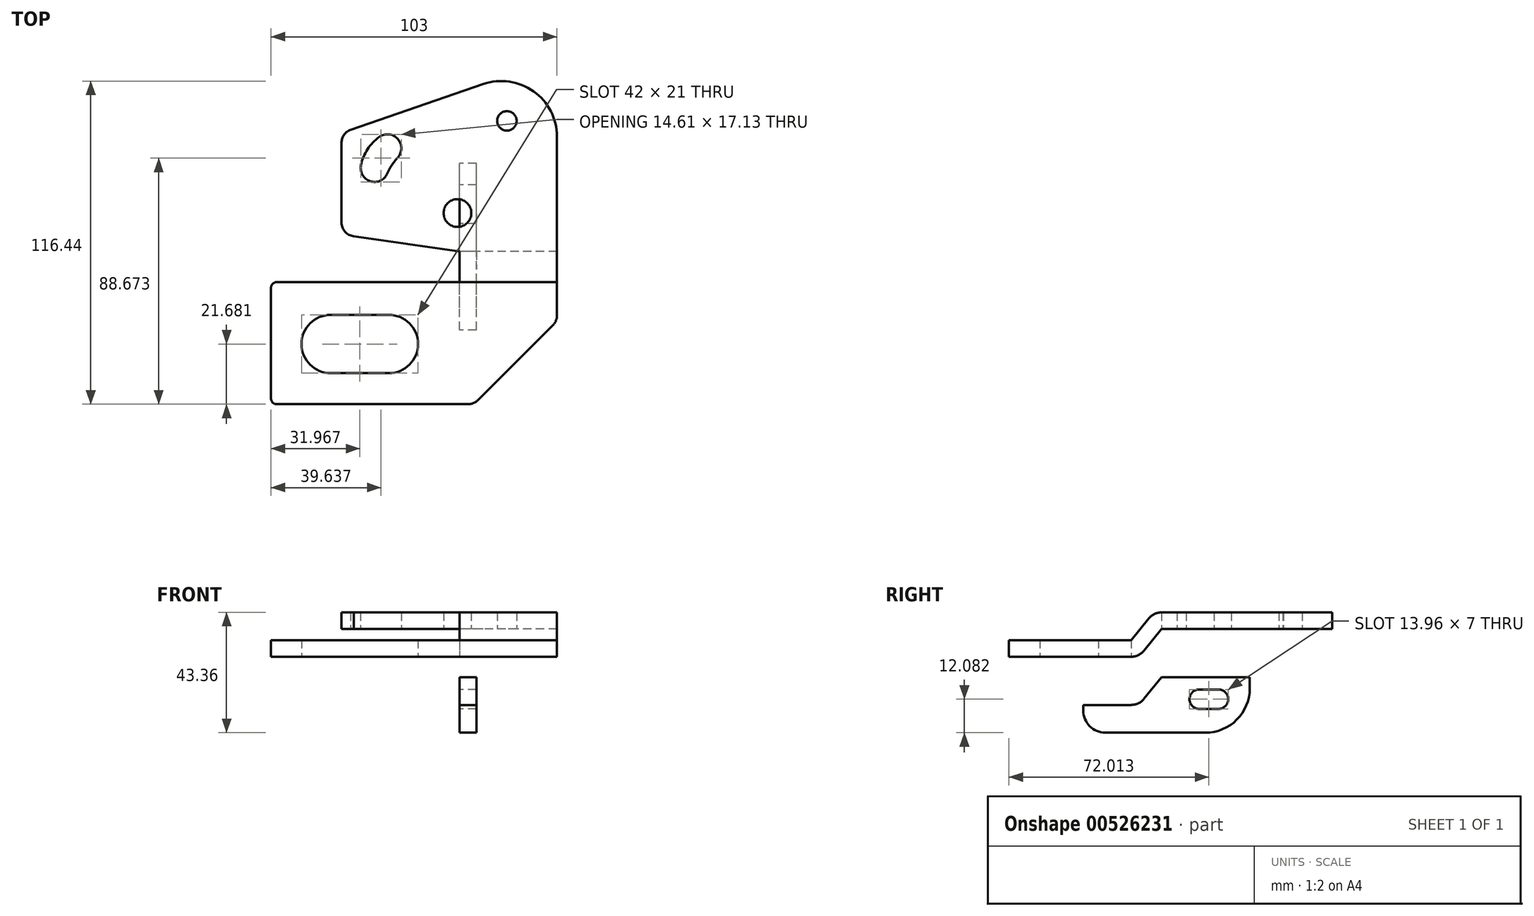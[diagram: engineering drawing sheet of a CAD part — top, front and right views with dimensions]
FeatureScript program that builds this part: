
annotation { "Feature Type Name" : "Feature", "Feature Type Description" : "" }
export const myFeature = defineFeature(function(context is Context, id is Id, definition is map)
    precondition{}
    {
        {
            var Q0;
            Q0=qCreatedBy(makeId("Top.planeOp"),FACE);
            var sketch = newSketch(context, id + "F0", { "sketchPlane" : qUnion([Q0])});
            skLineSegment(sketch, "E0.bottom", {"start": v(-65.96, -11) * mm, "end": v(0, -11) * mm});
            skLineSegment(sketch, "E0.top", {"start": v(-65.96, -55) * mm, "end": v(2.96, -55) * mm});
            skLineSegment(sketch, "E0.left", {"start": v(-67.96, -13) * mm, "end": v(-67.96, -53) * mm});
            skArc(sketch, "E1", {"start": v(-46.5, -22.82) * mm, "mid": v(-57, -33.32) * mm, "end": v(-46.5, -43.82) * mm});
            skArc(sketch, "E2", {"start": v(-25.5, -43.82) * mm, "mid": v(-15, -33.32) * mm, "end": v(-25.5, -22.82) * mm});
            skLineSegment(sketch, "E3", {"start": v(-46.5, -22.82) * mm, "end": v(-25.5, -22.82) * mm});
            skLineSegment(sketch, "E4", {"start": v(-46.5, -43.82) * mm, "end": v(-25.5, -43.82) * mm});
            skLineSegment(sketch, "E5", {"start": v(33.57, -26.5) * mm, "end": v(6.5, -53.54) * mm});
            skLineSegment(sketch, "E6", {"start": v(-42.58, 39.2) * mm, "end": v(-42.58, 10.48) * mm});
            skArc(sketch, "E7.filletArc", {"start": v(-42.58, 10.48) * mm, "mid": v(-41.3, 7.15) * mm, "end": v(-38.14, 5.51) * mm});
            skArc(sketch, "E8.filletArc", {"start": v(33.57, -26.5) * mm, "mid": v(34.66, -24.88) * mm, "end": v(35.04, -22.96) * mm});
            skLineSegment(sketch, "E9", {"start": v(8.51, 60.35) * mm, "end": v(-39.29, 43.9) * mm});
            skArc(sketch, "E10.filletArc", {"start": v(-39.29, 43.9) * mm, "mid": v(-41.67, 42.06) * mm, "end": v(-42.58, 39.2) * mm});
            skArc(sketch, "E11.filletArc", {"start": v(2.96, -55) * mm, "mid": v(4.88, -54.62) * mm, "end": v(6.5, -53.54) * mm});
            skCircle(sketch, "E12", {"center": v(-0.8, 13.88) * mm, "radius": 5 * mm});
            skArc(sketch, "E13", {"start": v(-35.57, 31.16) * mm, "mid": v(-32.23, 25.34) * mm, "end": v(-26.1, 28.1) * mm});
            skArc(sketch, "E14", {"start": v(-22.33, 33.89) * mm, "mid": v(-22.3, 40.6) * mm, "end": v(-28.96, 41.3) * mm});
            skArc(sketch, "E15", {"start": v(-28.96, 41.3) * mm, "mid": v(-33.2, 36.84) * mm, "end": v(-35.57, 31.16) * mm});
            skArc(sketch, "E16", {"start": v(-22.33, 33.89) * mm, "mid": v(-24.46, 31.15) * mm, "end": v(-26.1, 28.1) * mm});
            skCircle(sketch, "E17", {"center": v(17, 47.09) * mm, "radius": 3.5 * mm});
            skArc(sketch, "E18.filletArc", {"start": v(-65.96, -11) * mm, "mid": v(-67.37, -11.59) * mm, "end": v(-67.96, -13) * mm});
            skArc(sketch, "E19.filletArc", {"start": v(-67.96, -53) * mm, "mid": v(-67.37, -54.41) * mm, "end": v(-65.96, -55) * mm});
            skLineSegment(sketch, "E20.trimOffspring", {"start": v(-38.14, 5.51) * mm, "end": v(0, 0) * mm});
            skArc(sketch, "E21", {"start": v(35.02, 41.44) * mm, "mid": v(26.64, 57.72) * mm, "end": v(8.51, 60.35) * mm});
            skLineSegment(sketch, "E22", {"start": v(0, -11) * mm, "end": v(0, 0) * mm});
            skLineSegment(sketch, "E23", {"start": v(35.02, 41.44) * mm, "end": v(35.04, -22.96) * mm});
            skSolve(sketch);
        }
        {
            var Q0;
            Q0=qCreatedBy(makeId("Right.planeOp"),FACE);
            var sketch = newSketch(context, id + "F1", { "sketchPlane" : qUnion([Q0])});
            skLineSegment(sketch, "E24.right", {"start": v(79.89, 0) * mm, "end": v(79.89, -6) * mm});
            skLineSegment(sketch, "E25", {"start": v(-11, -10) * mm, "end": v(-11, -16) * mm});
            skLineSegment(sketch, "E26", {"start": v(0, -6) * mm, "end": v(0, 0) * mm});
            skLineSegment(sketch, "E27", {"start": v(0, 0) * mm, "end": v(0, -6) * mm});
            skLineSegment(sketch, "E28.trimOffspring", {"start": v(0, -6) * mm, "end": v(79.89, -6) * mm});
            skLineSegment(sketch, "E29.trimOffspring", {"start": v(0, 0) * mm, "end": v(79.89, 0) * mm});
            skArc(sketch, "E30", {"start": v(-11, -16) * mm, "mid": v(-8.43, -15.42) * mm, "end": v(-6.35, -13.8) * mm});
            skArc(sketch, "E31", {"start": v(0, 0) * mm, "mid": v(-2.57, -0.58) * mm, "end": v(-4.65, -2.2) * mm});
            skLineSegment(sketch, "E32", {"start": v(-11, -10) * mm, "end": v(-4.65, -2.2) * mm});
            skLineSegment(sketch, "E33", {"start": v(0, -6) * mm, "end": v(-6.35, -13.8) * mm});
            skLineSegment(sketch, "E34", {"start": v(-67.68, -10) * mm, "end": v(-67.68, -16) * mm});
            skLineSegment(sketch, "E35", {"start": v(-67.68, -16) * mm, "end": v(-11, -16) * mm});
            skLineSegment(sketch, "E36", {"start": v(-67.68, -10) * mm, "end": v(-11, -10) * mm});
            skLineSegment(sketch, "E37.trimOffspring", {"start": v(0, -23.36) * mm, "end": v(31.77, -23.36) * mm});
            skArc(sketch, "E38", {"start": v(-11, -33.36) * mm, "mid": v(-8.43, -32.77) * mm, "end": v(-6.35, -31.15) * mm});
            skLineSegment(sketch, "E39", {"start": v(0, -23.36) * mm, "end": v(-6.35, -31.15) * mm});
            skLineSegment(sketch, "E40", {"start": v(-28.23, -33.36) * mm, "end": v(-11, -33.36) * mm});
            skLineSegment(sketch, "E41", {"start": v(-28.23, -33.36) * mm, "end": v(-28.23, -35.36) * mm});
            skLineSegment(sketch, "E42", {"start": v(-20.23, -43.36) * mm, "end": v(15.77, -43.36) * mm});
            skArc(sketch, "E43.filletArc", {"start": v(-28.23, -35.36) * mm, "mid": v(-25.9, -41.01) * mm, "end": v(-20.23, -43.36) * mm});
            skArc(sketch, "E44.filletArc", {"start": v(15.77, -43.36) * mm, "mid": v(27.08, -38.67) * mm, "end": v(31.77, -27.36) * mm});
            skLineSegment(sketch, "E45", {"start": v(31.77, -27.36) * mm, "end": v(31.77, -23.36) * mm});
            skArc(sketch, "E46", {"start": v(13.54, -27.78) * mm, "mid": v(10.04, -31.28) * mm, "end": v(13.54, -34.78) * mm});
            skArc(sketch, "E47", {"start": v(20.5, -34.78) * mm, "mid": v(24, -31.28) * mm, "end": v(20.5, -27.78) * mm});
            skLineSegment(sketch, "E48", {"start": v(13.54, -27.78) * mm, "end": v(20.5, -27.78) * mm});
            skLineSegment(sketch, "E49", {"start": v(13.54, -34.78) * mm, "end": v(20.5, -34.78) * mm});
            skSolve(sketch);
        }
        {
            var Q0;
            Q0=makeQuery(id+"F0.imprint","IMPRINT",FACE,{"disambiguationData":[TD([[makeQuery(id+"F0.imprint","IMPRINT",EDGE,{"derivedFrom":sQuery(id+"F0.wireOp",EDGE,"E0.left")}),1.0]])]});
            extrude(context, id + "F2", {"entities" : qUnion([Q0]), "endBound" : BoundingType.SYMMETRIC, "depth" : 100 * mm, "offsetDistance" : 25 * mm});
        }
        {
            var Q0;
            Q0=makeQuery(id+"F1.imprint","IMPRINT",FACE,{"disambiguationData":[TD([[makeQuery(id+"F1.imprint","IMPRINT",EDGE,{"derivedFrom":sQuery(id+"F1.wireOp",EDGE,"E25")}),-1.0]])]});
            var Q1;
            Q1=makeQuery(id+"F1.imprint","IMPRINT",FACE,{"disambiguationData":[TD([[makeQuery(id+"F1.imprint","IMPRINT",EDGE,{"derivedFrom":sQuery(id+"F1.wireOp",EDGE,"E25")}),1.0]])]});
            var Q2;
            Q2=makeQuery(id+"F1.imprint","IMPRINT",FACE,{"disambiguationData":[TD([[makeQuery(id+"F1.imprint","IMPRINT",EDGE,{"derivedFrom":sQuery(id+"F1.wireOp",EDGE,"E24.right")}),-1.0]])]});
            extrude(context, id + "F3", {"entities" : qUnion([Q0, Q1, Q2]), "operationType" : NewBodyOperationType.INTERSECT, "endBound" : BoundingType.SYMMETRIC, "depth" : 200 * mm, "offsetDistance" : 25 * mm});
        }
        {
            var Q0;
            Q0=makeQuery(id+"F1.imprint","IMPRINT",FACE,{"disambiguationData":[TD([[makeQuery(id+"F1.imprint","IMPRINT",EDGE,{"derivedFrom":sQuery(id+"F1.wireOp",EDGE,"E37.trimOffspring")}),-1.0]])]});
            extrude(context, id + "F4", {"entities" : qUnion([Q0]), "depth" : 6 * mm, "offsetDistance" : 25 * mm});
        }
    });
